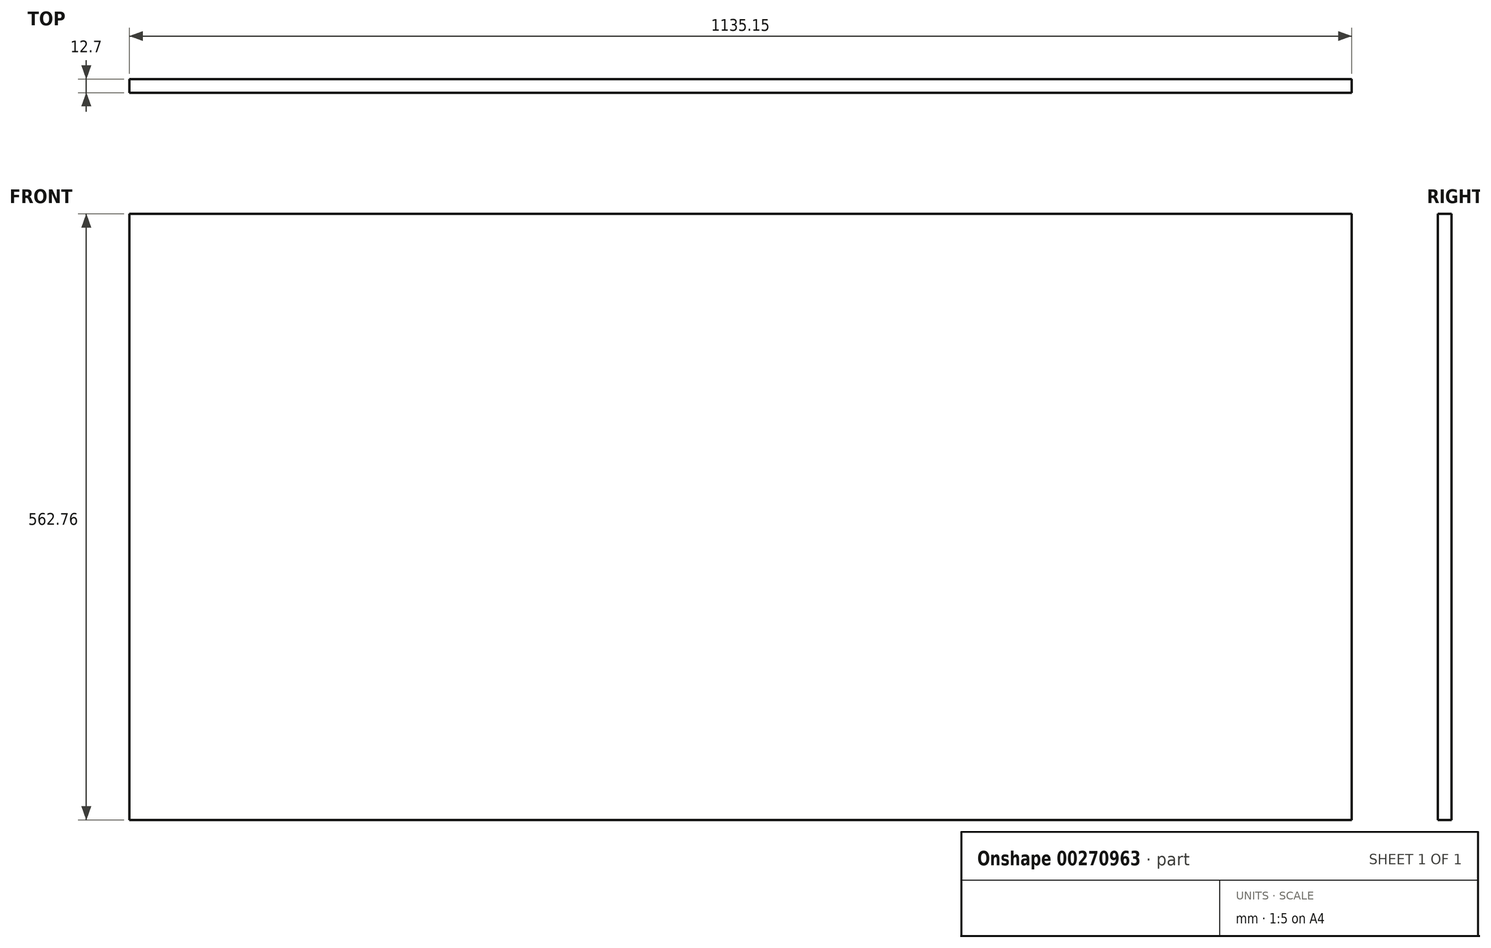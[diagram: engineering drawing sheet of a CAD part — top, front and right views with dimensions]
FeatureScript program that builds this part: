
annotation { "Feature Type Name" : "Feature", "Feature Type Description" : "" }
export const myFeature = defineFeature(function(context is Context, id is Id, definition is map)
    precondition{}
    {
        {
            var Q0;
            Q0=qCreatedBy(makeId("Front.planeOp"),FACE);
            var sketch = newSketch(context, id + "F0", { "sketchPlane" : qUnion([Q0])});
            skLineSegment(sketch, "E0", {"start": v(0, 0) * mm, "end": v(0, 562.76) * mm});
            skLineSegment(sketch, "E1", {"start": v(0, 562.76) * mm, "end": v(1135.15, 562.76) * mm});
            skLineSegment(sketch, "E2", {"start": v(1135.15, 562.76) * mm, "end": v(1135.15, 0) * mm});
            skLineSegment(sketch, "E3", {"start": v(1135.15, 0) * mm, "end": v(0, 0) * mm});
            skSolve(sketch);
        }
        {
            var Q0;
            Q0 = qSketchRegion(id + "F0", true);
            extrude(context, id + "F1", {"entities" : qUnion([Q0]), "depth" : 12.7 * mm});
        }
    });
